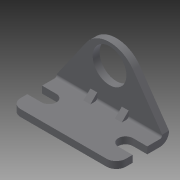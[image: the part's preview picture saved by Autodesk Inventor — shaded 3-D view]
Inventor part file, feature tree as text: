
AUTODESK INVENTOR PART (.ipt)
format: ipt  version: 2013 (Build 170138000, 138)  size: 187,392 bytes
history: native  units: in
note: dims shown in document units (in); Inventor stores cm internally (conversion verified against a paired STEP export)
features: other x126, sketch x9, extrude x8, hole x1
ambient origin geometry x8: Origin, YZ Plane, XZ Plane, XY Plane, X Axis, Y Axis, Z Axis, Center Point
bodies: Solid1 (feature_tree)
feature tree (144):
  extrude  "Extrusion1"  Depth=0.1346in TaperAngle=0.0deg
  extrude  "Extrusion2"  Depth=0.1346in TaperAngle=0.0deg
  hole  "Drilling 1"  [1 undecoded]
  extrude  "Extrusion3"  Depth=0.0897in TaperAngle=0.0deg
  extrude  "Extrusion4"  [1 undecoded]
  extrude  "Extrusion5"  [1 undecoded]
  extrude  "Extrusion6"  [1 undecoded]
  extrude  "Extrusion7"  [1 undecoded]
  extrude  "Extrusion8"  [1 undecoded]
  other  "h1_XY"
  other  "h1_YZ"
  other  "h1_ZX"
  other  "h1_X"
  other  "h1_Y"
  other  "h1_Z"
  other  "h1_Center"
  other  "d1_XY"
  other  "d1_YZ"
  other  "d1_ZX"
  other  "d1_X"
  other  "d1_Y"
  other  "d1_Z"
  other  "d1_Center"
  other  "h2_XY"
  other  "h2_YZ"
  other  "h2_ZX"
  other  "h2_X"
  other  "h2_Y"
  other  "h2_Z"
  other  "h2_Center"
  other  "d2_XY"
  other  "d2_YZ"
  other  "d2_ZX"
  other  "d2_X"
  other  "d2_Y"
  other  "d2_Z"
  other  "d2_Center"
  other  "h3_XY"
  other  "h3_YZ"
  other  "h3_ZX"
  other  "h3_X"
  other  "h3_Y"
  other  "h3_Z"
  other  "h3_Center"
  other  "h4_XY"
  other  "h4_YZ"
  other  "h4_ZX"
  other  "h4_X"
  other  "h4_Y"
  other  "h4_Z"
  other  "h4_Center"
  other  "h5_XY"
  other  "h5_YZ"
  other  "h5_ZX"
  other  "h5_X"
  other  "h5_Y"
  other  "h5_Z"
  other  "h5_Center"
  other  "h6_XY"
  other  "h6_YZ"
  other  "h6_ZX"
  other  "h6_X"
  other  "h6_Y"
  other  "h6_Z"
  other  "h6_Center"
  other  "l1_XY"
  other  "l1_YZ"
  other  "l1_ZX"
  other  "l1_X"
  other  "l1_Y"
  other  "l1_Z"
  other  "l1_Center"
  other  "l2_XY"
  other  "l2_YZ"
  other  "l2_ZX"
  other  "l2_X"
  other  "l2_Y"
  other  "l2_Z"
  other  "l2_Center"
  other  "l3_XY"
  other  "l3_YZ"
  other  "l3_ZX"
  other  "l3_X"
  other  "l3_Y"
  other  "l3_Z"
  other  "l3_Center"
  other  "l4_XY"
  other  "l4_YZ"
  other  "l4_ZX"
  other  "l4_X"
  other  "l4_Y"
  other  "l4_Z"
  other  "l4_Center"
  other  "l5_XY"
  other  "l5_YZ"
  other  "l5_ZX"
  other  "l5_X"
  other  "l5_Y"
  other  "l5_Z"
  other  "l5_Center"
  other  "l6_XY"
  other  "l6_YZ"
  other  "l6_ZX"
  other  "l6_X"
  other  "l6_Y"
  other  "l6_Z"
  other  "l6_Center"
  other  "l7_XY"
  other  "l7_YZ"
  other  "l7_ZX"
  other  "l7_X"
  other  "l7_Y"
  other  "l7_Z"
  other  "l7_Center"
  other  "l8_XY"
  other  "l8_YZ"
  other  "l8_ZX"
  other  "l8_X"
  other  "l8_Y"
  other  "l8_Z"
  other  "l8_Center"
  other  "mounting_bracket_XY"
  other  "mounting_bracket_YZ"
  other  "mounting_bracket_ZX"
  other  "mounting_bracket_X"
  other  "mounting_bracket_Y"
  other  "mounting_bracket_Z"
  other  "mounting_bracket_Center"
  other  "mounting_bracket_1_XY"
  other  "mounting_bracket_1_YZ"
  other  "mounting_bracket_1_ZX"
  other  "mounting_bracket_1_X"
  other  "mounting_bracket_1_Y"
  other  "mounting_bracket_1_Z"
  other  "mounting_bracket_1_Center"
  sketch  "Sketch_1"  dims[d0=1.375in d1=0.0in d2=0.1346in d3=0.0in]
  sketch  "Sketch_2"  dims[d4=0.4405in d5=0.75in d6=0.375in d7=0.25in d8=0.5635in d9=0.1346in d10=0.0in d11=0.1346in d12=0.0in]
  sketch  "Sketch3"  dims[d13=0.1346in d14=0.0in d15=0.1346in d16=0.0in]
  sketch  "Sketch_6"  dims[d17=0.1346in d18=0.0in d19=0.0897in d20=0.0in]
  sketch  "Sketch_7"  dims[d21=0.0897in d22=0.0in]
  sketch  "Sketch_8"
  sketch  "Sketch_9"
  sketch  "Sketch_10"
  sketch  "Sketch_14"
note: 6 required parameter values undecoded (feature->parameter linkage not recoverable at this tier; creation-order binding heuristic only, values carry confidence <= 0.55)
